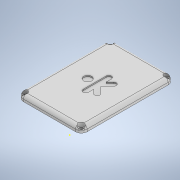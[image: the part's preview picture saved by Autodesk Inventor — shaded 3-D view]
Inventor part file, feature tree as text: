
AUTODESK INVENTOR PART (.ipt)
format: ipt  version: 2021 (Build 250183000, 183)  size: 312,832 bytes
history: native  units: mm
features: sketch x12, extrude x9, other x7, projected_geometry x3, fillet x1, shell x1
ambient origin geometry x8: Origin, YZ Plane, XZ Plane, XY Plane, X Axis, Y Axis, Z Axis, Center Point
bodies: Body1 (feature_tree)
feature tree (33):
  other  "솔리드1"
  extrude  "돌출1"  Depth=55.0mm
  fillet  "모깎기1"  Radius=90.0mm
  sketch  "스케치2"
  shell  "쉘1"  Thickness=10.0mm
  extrude  "돌출2"  Depth=5.0mm
  extrude  "돌출3"  Depth=3.0mm
  other  "스레드1"
  other  "스레드2"
  other  "스레드3"
  other  "스레드4"
  extrude  "돌출4"  Depth=5.0mm
  sketch  "스케치6"
  sketch  "스케치9"
  sketch  "스케치10"
  extrude  "돌출6"  Depth=5.0mm
  extrude  "돌출7"  Depth=5.0mm
  extrude  "돌출8"  Depth=5.0mm
  other  "직접 편집1"
  extrude  "돌출9"  Depth=5.0mm
  extrude  "돌출10"  Depth=3.0mm TaperAngle=0.0deg
  sketch  "스케치1"
  sketch  "스케치3"
  sketch  "스케치4"
  sketch  "스케치5"
  sketch  "스케치11"
  projected_geometry  "투영된 루프1"
  projected_geometry  "투영된 루프2"
  sketch  "스케치12"
  sketch  "스케치13"
  projected_geometry  "투영된 루프3"
  sketch  "스케치14"
  other  "이동1"
